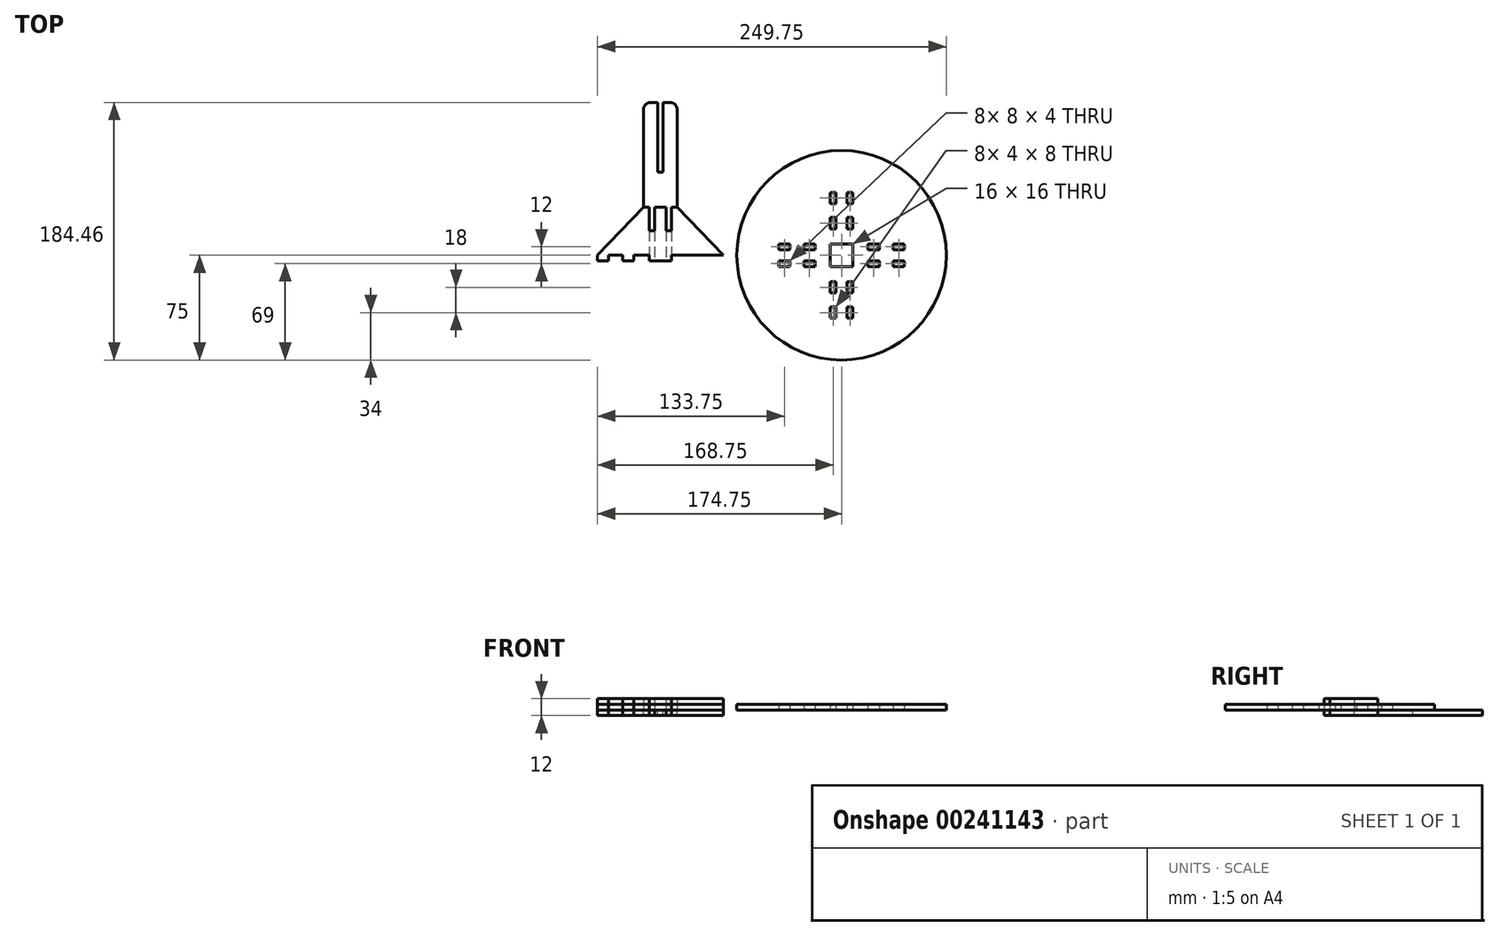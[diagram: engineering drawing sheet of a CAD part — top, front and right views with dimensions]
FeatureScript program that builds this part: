
annotation { "Feature Type Name" : "Feature", "Feature Type Description" : "" }
export const myFeature = defineFeature(function(context is Context, id is Id, definition is map)
    precondition{}
    {
        {
            var Q0;
            Q0=qCreatedBy(makeId("Top.planeOp"),FACE);
            var sketch = newSketch(context, id + "F0", { "sketchPlane" : qUnion([Q0])});
            skCircle(sketch, "E0", {"center": v(0, 0) * mm, "radius": 75 * mm});
            skLineSegment(sketch, "E1", {"start": v(-84.75, 0) * mm, "end": v(-129.75, 0) * mm});
            skLineSegment(sketch, "E2", {"start": v(-129.75, 0) * mm, "end": v(-129.75, 34.46) * mm});
            skLineSegment(sketch, "E3", {"start": v(-129.75, 34.46) * mm, "end": v(-117.75, 34.46) * mm});
            skLineSegment(sketch, "E4", {"start": v(-117.75, 34.46) * mm, "end": v(-84.75, 0) * mm});
            skLineSegment(sketch, "E5.top", {"start": v(-129.75, 17.59) * mm, "end": v(-125.75, 17.59) * mm});
            skLineSegment(sketch, "E5.right", {"start": v(-125.75, 34.46) * mm, "end": v(-125.75, 17.59) * mm});
            skLineSegment(sketch, "E6.bottom", {"start": v(-125.75, 34.46) * mm, "end": v(-121.75, 34.46) * mm});
            skLineSegment(sketch, "E6.top", {"start": v(-125.75, 0) * mm, "end": v(-121.75, 0) * mm});
            skLineSegment(sketch, "E6.left", {"start": v(-125.75, 34.46) * mm, "end": v(-125.75, 0) * mm});
            skLineSegment(sketch, "E6.right", {"start": v(-121.75, 34.46) * mm, "end": v(-121.75, 0) * mm});
            skLineSegment(sketch, "E7", {"start": v(-125.75, 17.59) * mm, "end": v(-121.75, 17.59) * mm});
            skLineSegment(sketch, "E8.bottom", {"start": v(-129.75, 0) * mm, "end": v(-121.75, 0) * mm});
            skLineSegment(sketch, "E8.top", {"start": v(-129.75, -4) * mm, "end": v(-121.75, -4) * mm});
            skLineSegment(sketch, "E8.left", {"start": v(-129.75, 0) * mm, "end": v(-129.75, -4) * mm});
            skLineSegment(sketch, "E8.right", {"start": v(-121.75, 0) * mm, "end": v(-121.75, -4) * mm});
            skLineSegment(sketch, "E9.bottom", {"start": v(-84.75, 0) * mm, "end": v(-92.75, 0) * mm});
            skLineSegment(sketch, "E9.top", {"start": v(-84.75, -4) * mm, "end": v(-92.75, -4) * mm});
            skLineSegment(sketch, "E9.left", {"start": v(-84.75, 0) * mm, "end": v(-84.75, -4) * mm});
            skLineSegment(sketch, "E9.right", {"start": v(-92.75, 0) * mm, "end": v(-92.75, -4) * mm});
            skLineSegment(sketch, "E10.bottom", {"start": v(-102.75, 0) * mm, "end": v(-110.75, 0) * mm});
            skLineSegment(sketch, "E10.top", {"start": v(-102.75, -4) * mm, "end": v(-110.75, -4) * mm});
            skLineSegment(sketch, "E10.left", {"start": v(-102.75, 0) * mm, "end": v(-102.75, -4) * mm});
            skLineSegment(sketch, "E10.right", {"start": v(-110.75, 0) * mm, "end": v(-110.75, -4) * mm});
            skLineSegment(sketch, "E11.MirrorCS", {"start": v(-174.75, 0) * mm, "end": v(-174.75, -4) * mm});
            skLineSegment(sketch, "E12.MirrorCS", {"start": v(-156.75, 0) * mm, "end": v(-156.75, -4) * mm});
            skLineSegment(sketch, "E13.MirrorCS", {"start": v(-148.75, 0) * mm, "end": v(-148.75, -4) * mm});
            skLineSegment(sketch, "E14.MirrorCS", {"start": v(-166.75, 0) * mm, "end": v(-166.75, -4) * mm});
            skLineSegment(sketch, "E15.MirrorCS", {"start": v(-137.75, 0) * mm, "end": v(-137.75, -4) * mm});
            skLineSegment(sketch, "E16.MirrorCS", {"start": v(-129.75, 0) * mm, "end": v(-137.75, 0) * mm});
            skLineSegment(sketch, "E17.MirrorCS", {"start": v(-133.75, 0) * mm, "end": v(-137.75, 0) * mm});
            skLineSegment(sketch, "E18.MirrorCS", {"start": v(-133.75, 34.46) * mm, "end": v(-137.75, 34.46) * mm});
            skLineSegment(sketch, "E19.MirrorCS", {"start": v(-129.75, 34.46) * mm, "end": v(-141.75, 34.46) * mm});
            skLineSegment(sketch, "E20.MirrorCS", {"start": v(-133.75, 17.59) * mm, "end": v(-137.75, 17.59) * mm});
            skLineSegment(sketch, "E21.MirrorCS", {"start": v(-129.75, 17.59) * mm, "end": v(-133.75, 17.59) * mm});
            skLineSegment(sketch, "E22.MirrorCS", {"start": v(-133.75, 34.46) * mm, "end": v(-133.75, 17.59) * mm});
            skLineSegment(sketch, "E23.MirrorCS", {"start": v(-156.75, -4) * mm, "end": v(-148.75, -4) * mm});
            skLineSegment(sketch, "E24.MirrorCS", {"start": v(-174.75, 0) * mm, "end": v(-166.75, 0) * mm});
            skLineSegment(sketch, "E25.MirrorCS", {"start": v(-156.75, 0) * mm, "end": v(-148.75, 0) * mm});
            skLineSegment(sketch, "E26.MirrorCS", {"start": v(-174.75, -4) * mm, "end": v(-166.75, -4) * mm});
            skLineSegment(sketch, "E27.MirrorCS", {"start": v(-129.75, -4) * mm, "end": v(-137.75, -4) * mm});
            skLineSegment(sketch, "E28.MirrorCS", {"start": v(-137.75, 34.46) * mm, "end": v(-137.75, 0) * mm});
            skLineSegment(sketch, "E29.MirrorCS", {"start": v(-133.75, 34.46) * mm, "end": v(-133.75, 0) * mm});
            skLineSegment(sketch, "E30.MirrorCS", {"start": v(-174.75, 0) * mm, "end": v(-129.75, 0) * mm});
            skLineSegment(sketch, "E31.MirrorCS", {"start": v(-141.75, 34.46) * mm, "end": v(-174.75, 0) * mm});
            skLineSegment(sketch, "E32", {"start": v(-133.75, 0) * mm, "end": v(-133.75, -4) * mm});
            skLineSegment(sketch, "E33", {"start": v(-125.75, 0) * mm, "end": v(-125.75, -4) * mm});
            skLineSegment(sketch, "E34.bottom", {"start": v(8, 4) * mm, "end": v(-8, 4) * mm, "construction": true});
            skLineSegment(sketch, "E34.top", {"start": v(8, -4) * mm, "end": v(-8, -4) * mm, "construction": true});
            skLineSegment(sketch, "E34.left", {"start": v(8, 4) * mm, "end": v(8, -4) * mm, "construction": true});
            skLineSegment(sketch, "E34.right", {"start": v(-8, 4) * mm, "end": v(-8, -4) * mm, "construction": true});
            skLineSegment(sketch, "E35.bottom", {"start": v(-8, 4) * mm, "end": v(8, 4) * mm});
            skLineSegment(sketch, "E35.top", {"start": v(-8, 8) * mm, "end": v(8, 8) * mm});
            skLineSegment(sketch, "E35.left", {"start": v(-8, 4) * mm, "end": v(-8, 8) * mm});
            skLineSegment(sketch, "E35.right", {"start": v(8, 4) * mm, "end": v(8, 8) * mm});
            skLineSegment(sketch, "E36", {"start": v(8, 8) * mm, "end": v(19, 8) * mm, "construction": true});
            skLineSegment(sketch, "E37", {"start": v(19, 8) * mm, "end": v(8, 0) * mm, "construction": true});
            skLineSegment(sketch, "E38", {"start": v(8, 0) * mm, "end": v(-47.74, 0) * mm, "construction": true});
            skLineSegment(sketch, "E39.bottom", {"start": v(19, 8) * mm, "end": v(27, 8) * mm});
            skLineSegment(sketch, "E39.top", {"start": v(19, 4) * mm, "end": v(27, 4) * mm});
            skLineSegment(sketch, "E39.left", {"start": v(19, 8) * mm, "end": v(19, 4) * mm});
            skLineSegment(sketch, "E39.right", {"start": v(27, 8) * mm, "end": v(27, 4) * mm});
            skLineSegment(sketch, "E40", {"start": v(27, 8) * mm, "end": v(37, 8) * mm, "construction": true});
            skLineSegment(sketch, "E41.bottom", {"start": v(37, 8) * mm, "end": v(45, 8) * mm});
            skLineSegment(sketch, "E41.top", {"start": v(37, 4) * mm, "end": v(45, 4) * mm});
            skLineSegment(sketch, "E41.left", {"start": v(37, 8) * mm, "end": v(37, 4) * mm});
            skLineSegment(sketch, "E41.right", {"start": v(45, 8) * mm, "end": v(45, 4) * mm});
            skLineSegment(sketch, "E42", {"start": v(0, 8) * mm, "end": v(0, -16.73) * mm, "construction": true});
            skPoint(sketch, "E42.endSnap0", {"position": v(0, 8) * mm});
            skLineSegment(sketch, "E43.MirrorCS", {"start": v(-45, 8) * mm, "end": v(-45, 4) * mm});
            skLineSegment(sketch, "E44.MirrorCS", {"start": v(-19, 8) * mm, "end": v(-19, 4) * mm});
            skLineSegment(sketch, "E45.MirrorCS", {"start": v(-27, 8) * mm, "end": v(-27, 4) * mm});
            skLineSegment(sketch, "E46.MirrorCS", {"start": v(-37, 8) * mm, "end": v(-37, 4) * mm});
            skLineSegment(sketch, "E47.MirrorCS", {"start": v(-19, 8) * mm, "end": v(-27, 8) * mm});
            skLineSegment(sketch, "E48.MirrorCS", {"start": v(-19, 4) * mm, "end": v(-27, 4) * mm});
            skLineSegment(sketch, "E49.MirrorCS", {"start": v(-37, 4) * mm, "end": v(-45, 4) * mm});
            skLineSegment(sketch, "E50.MirrorCS", {"start": v(-37, 8) * mm, "end": v(-45, 8) * mm});
            skLineSegment(sketch, "E51.MirrorCS", {"start": v(-27, 8) * mm, "end": v(-37, 8) * mm, "construction": true});
            skLineSegment(sketch, "E52.MirrorCS", {"start": v(8, -4) * mm, "end": v(8, -8) * mm});
            skLineSegment(sketch, "E53.MirrorCS", {"start": v(-27, -8) * mm, "end": v(-27, -4) * mm});
            skLineSegment(sketch, "E54.MirrorCS", {"start": v(27, -8) * mm, "end": v(27, -4) * mm});
            skLineSegment(sketch, "E55.MirrorCS", {"start": v(-45, -8) * mm, "end": v(-45, -4) * mm});
            skLineSegment(sketch, "E56.MirrorCS", {"start": v(19, -8) * mm, "end": v(19, -4) * mm});
            skLineSegment(sketch, "E57.MirrorCS", {"start": v(-19, -8) * mm, "end": v(-19, -4) * mm});
            skLineSegment(sketch, "E58.MirrorCS", {"start": v(-8, -4) * mm, "end": v(-8, -8) * mm});
            skLineSegment(sketch, "E59.MirrorCS", {"start": v(37, -8) * mm, "end": v(37, -4) * mm});
            skLineSegment(sketch, "E60.MirrorCS", {"start": v(45, -8) * mm, "end": v(45, -4) * mm});
            skLineSegment(sketch, "E61.MirrorCS", {"start": v(-37, -8) * mm, "end": v(-37, -4) * mm});
            skLineSegment(sketch, "E62.MirrorCS", {"start": v(-8, -4) * mm, "end": v(8, -4) * mm});
            skLineSegment(sketch, "E63.MirrorCS", {"start": v(19, -8) * mm, "end": v(27, -8) * mm});
            skLineSegment(sketch, "E64.MirrorCS", {"start": v(19, -4) * mm, "end": v(27, -4) * mm});
            skLineSegment(sketch, "E65.MirrorCS", {"start": v(-37, -8) * mm, "end": v(-45, -8) * mm});
            skLineSegment(sketch, "E66.MirrorCS", {"start": v(-8, -8) * mm, "end": v(8, -8) * mm});
            skLineSegment(sketch, "E67.MirrorCS", {"start": v(-37, -4) * mm, "end": v(-45, -4) * mm});
            skLineSegment(sketch, "E68.MirrorCS", {"start": v(-27, -8) * mm, "end": v(-37, -8) * mm, "construction": true});
            skPoint(sketch, "E69.MirrorP", {"position": v(0, -8) * mm});
            skLineSegment(sketch, "E70.MirrorCS", {"start": v(27, -8) * mm, "end": v(37, -8) * mm, "construction": true});
            skLineSegment(sketch, "E71.MirrorCS", {"start": v(37, -8) * mm, "end": v(45, -8) * mm});
            skLineSegment(sketch, "E72.MirrorCS", {"start": v(-19, -8) * mm, "end": v(-27, -8) * mm});
            skLineSegment(sketch, "E73.MirrorCS", {"start": v(-19, -4) * mm, "end": v(-27, -4) * mm});
            skLineSegment(sketch, "E74.MirrorCS", {"start": v(8, -8) * mm, "end": v(19, -8) * mm, "construction": true});
            skLineSegment(sketch, "E75.MirrorCS", {"start": v(37, -4) * mm, "end": v(45, -4) * mm});
            skLineSegment(sketch, "E76.bottom", {"start": v(-8, 4) * mm, "end": v(-4, 4) * mm});
            skLineSegment(sketch, "E76.top", {"start": v(-8, -4) * mm, "end": v(-4, -4) * mm});
            skLineSegment(sketch, "E76.left", {"start": v(-8, 4) * mm, "end": v(-8, -4) * mm});
            skLineSegment(sketch, "E76.right", {"start": v(-4, 4) * mm, "end": v(-4, -4) * mm});
            skLineSegment(sketch, "E77.bottom", {"start": v(8, 4) * mm, "end": v(8, 4) * mm});
            skLineSegment(sketch, "E77.top", {"start": v(8, -4) * mm, "end": v(8, -4) * mm});
            skLineSegment(sketch, "E77.left", {"start": v(8, 4) * mm, "end": v(8, -4) * mm});
            skLineSegment(sketch, "E77.right", {"start": v(8, 4) * mm, "end": v(8, -4) * mm});
            skLineSegment(sketch, "E78", {"start": v(-8, 8) * mm, "end": v(-8, 19) * mm, "construction": true});
            skLineSegment(sketch, "E79", {"start": v(-8, 19) * mm, "end": v(-8, 27) * mm, "construction": true});
            skLineSegment(sketch, "E80.bottom", {"start": v(-8, 27) * mm, "end": v(-4, 27) * mm});
            skLineSegment(sketch, "E80.top", {"start": v(-8, 19) * mm, "end": v(-4, 19) * mm});
            skLineSegment(sketch, "E80.left", {"start": v(-8, 27) * mm, "end": v(-8, 19) * mm});
            skLineSegment(sketch, "E80.right", {"start": v(-4, 27) * mm, "end": v(-4, 19) * mm});
            skLineSegment(sketch, "E81.bottom", {"start": v(-8, 37) * mm, "end": v(-4, 37) * mm});
            skLineSegment(sketch, "E81.top", {"start": v(-8, 45) * mm, "end": v(-4, 45) * mm});
            skLineSegment(sketch, "E81.left", {"start": v(-8, 37) * mm, "end": v(-8, 45) * mm});
            skLineSegment(sketch, "E81.right", {"start": v(-4, 37) * mm, "end": v(-4, 45) * mm});
            skLineSegment(sketch, "E82.MirrorCS", {"start": v(-8, -27) * mm, "end": v(-4, -27) * mm});
            skLineSegment(sketch, "E83.MirrorCS", {"start": v(-8, -19) * mm, "end": v(-4, -19) * mm});
            skLineSegment(sketch, "E84.MirrorCS", {"start": v(-8, -27) * mm, "end": v(-8, -19) * mm});
            skLineSegment(sketch, "E85.MirrorCS", {"start": v(-8, -37) * mm, "end": v(-8, -45) * mm});
            skLineSegment(sketch, "E86.MirrorCS", {"start": v(-4, -37) * mm, "end": v(-4, -45) * mm});
            skLineSegment(sketch, "E87.MirrorCS", {"start": v(-8, -45) * mm, "end": v(-4, -45) * mm});
            skLineSegment(sketch, "E88.MirrorCS", {"start": v(-8, -19) * mm, "end": v(-8, -27) * mm, "construction": true});
            skLineSegment(sketch, "E89.MirrorCS", {"start": v(-8, -37) * mm, "end": v(-4, -37) * mm});
            skLineSegment(sketch, "E90.MirrorCS", {"start": v(-4, -27) * mm, "end": v(-4, -19) * mm});
            skLineSegment(sketch, "E91.MirrorCS", {"start": v(8, 27) * mm, "end": v(4, 27) * mm});
            skLineSegment(sketch, "E92.MirrorCS", {"start": v(8, 37) * mm, "end": v(4, 37) * mm});
            skLineSegment(sketch, "E93.MirrorCS", {"start": v(8, 45) * mm, "end": v(4, 45) * mm});
            skLineSegment(sketch, "E94.MirrorCS", {"start": v(8, 19) * mm, "end": v(4, 19) * mm});
            skLineSegment(sketch, "E95.MirrorCS", {"start": v(8, 27) * mm, "end": v(8, 19) * mm});
            skLineSegment(sketch, "E96.MirrorCS", {"start": v(4, 37) * mm, "end": v(4, 45) * mm});
            skLineSegment(sketch, "E97.MirrorCS", {"start": v(8, 19) * mm, "end": v(8, 27) * mm, "construction": true});
            skLineSegment(sketch, "E98.MirrorCS", {"start": v(4, 27) * mm, "end": v(4, 19) * mm});
            skLineSegment(sketch, "E99.MirrorCS", {"start": v(8, 37) * mm, "end": v(8, 45) * mm});
            skLineSegment(sketch, "E100.MirrorCS", {"start": v(4, 4) * mm, "end": v(4, -4) * mm});
            skLineSegment(sketch, "E101.MirrorCS", {"start": v(8, -45) * mm, "end": v(4, -45) * mm});
            skLineSegment(sketch, "E102.MirrorCS", {"start": v(8, -19) * mm, "end": v(4, -19) * mm});
            skLineSegment(sketch, "E103.MirrorCS", {"start": v(8, -37) * mm, "end": v(4, -37) * mm});
            skLineSegment(sketch, "E104.MirrorCS", {"start": v(8, -27) * mm, "end": v(8, -19) * mm});
            skLineSegment(sketch, "E105.MirrorCS", {"start": v(4, -37) * mm, "end": v(4, -45) * mm});
            skLineSegment(sketch, "E106.MirrorCS", {"start": v(8, -37) * mm, "end": v(8, -45) * mm});
            skLineSegment(sketch, "E107.MirrorCS", {"start": v(8, -27) * mm, "end": v(4, -27) * mm});
            skLineSegment(sketch, "E108.MirrorCS", {"start": v(4, -27) * mm, "end": v(4, -19) * mm});
            skLineSegment(sketch, "E109.MirrorCS", {"start": v(8, -19) * mm, "end": v(8, -27) * mm, "construction": true});
            skLineSegment(sketch, "E110.bottom", {"start": v(-141.75, 34.46) * mm, "end": v(-117.75, 34.46) * mm});
            skLineSegment(sketch, "E110.top", {"start": v(-136.75, 109.46) * mm, "end": v(-122.75, 109.46) * mm});
            skLineSegment(sketch, "E110.left", {"start": v(-141.75, 34.46) * mm, "end": v(-141.75, 104.46) * mm});
            skLineSegment(sketch, "E110.right", {"start": v(-117.75, 34.46) * mm, "end": v(-117.75, 104.46) * mm});
            skLineSegment(sketch, "E111.bottom", {"start": v(-129.75, 109.46) * mm, "end": v(-127.75, 109.46) * mm});
            skLineSegment(sketch, "E111.top", {"start": v(-129.75, 59.46) * mm, "end": v(-127.75, 59.46) * mm});
            skLineSegment(sketch, "E111.left", {"start": v(-129.75, 109.46) * mm, "end": v(-129.75, 59.46) * mm});
            skLineSegment(sketch, "E111.right", {"start": v(-127.75, 109.46) * mm, "end": v(-127.75, 59.46) * mm});
            skLineSegment(sketch, "E112.MirrorCS", {"start": v(-131.75, 109.46) * mm, "end": v(-131.75, 59.46) * mm});
            skLineSegment(sketch, "E113.MirrorCS", {"start": v(-129.75, 59.46) * mm, "end": v(-131.75, 59.46) * mm});
            skPoint(sketch, "E114.visualSharp", {"position": v(-141.75, 109.46) * mm});
            skArc(sketch, "E114.filletArc", {"start": v(-136.75, 109.46) * mm, "mid": v(-140.29, 108) * mm, "end": v(-141.75, 104.46) * mm});
            skPoint(sketch, "E115.visualSharp", {"position": v(-117.75, 109.46) * mm});
            skArc(sketch, "E115.filletArc", {"start": v(-117.75, 104.46) * mm, "mid": v(-119.21, 108) * mm, "end": v(-122.75, 109.46) * mm});
            skSolve(sketch);
        }
        {
            var Q0;
            {var subQ0=sQuery(id+"F0.wireOp",EDGE,"E11.MirrorCS");Q0=makeQuery(id+"F0.imprint","IMPRINT",FACE,{"disambiguationData":[TD([[makeQuery(id+"F0.imprint","IMPRINT",EDGE,{"derivedFrom":subQ0}),1.0]])]});}
            var Q1;
            {var subQ0=sQuery(id+"F0.wireOp",EDGE,"E31.MirrorCS");Q1=makeQuery(id+"F0.imprint","IMPRINT",FACE,{"disambiguationData":[TD([[makeQuery(id+"F0.imprint","IMPRINT",EDGE,{"derivedFrom":subQ0}),1.0]])]});}
            var Q2;
            {var subQ0=sQuery(id+"F0.wireOp",EDGE,"E12.MirrorCS");Q2=makeQuery(id+"F0.imprint","IMPRINT",FACE,{"disambiguationData":[TD([[makeQuery(id+"F0.imprint","IMPRINT",EDGE,{"derivedFrom":subQ0}),1.0]])]});}
            var Q3;
            {var subQ0=sQuery(id+"F0.wireOp",EDGE,"E20.MirrorCS");Q3=makeQuery(id+"F0.imprint","IMPRINT",FACE,{"disambiguationData":[TD([[makeQuery(id+"F0.imprint","IMPRINT",EDGE,{"derivedFrom":subQ0}),1.0]])]});}
            var Q4;
            {var subQ3=sQuery(id+"F0.wireOp",EDGE,"E21.MirrorCS");Q4=makeQuery(id+"F0.imprint","IMPRINT",FACE,{"disambiguationData":[TD([[makeQuery(id+"F0.imprint","IMPRINT",EDGE,{"derivedFrom":subQ3}),1.0]])]});}
            var Q5;
            {var subQ3=sQuery(id+"F0.wireOp",EDGE,"E21.MirrorCS");Q5=makeQuery(id+"F0.imprint","IMPRINT",FACE,{"disambiguationData":[TD([[makeQuery(id+"F0.imprint","IMPRINT",EDGE,{"derivedFrom":subQ3}),-1.0]])]});}
            var Q6;
            {var subQ3=sQuery(id+"F0.wireOp",EDGE,"E5.top");Q6=makeQuery(id+"F0.imprint","IMPRINT",FACE,{"disambiguationData":[TD([[makeQuery(id+"F0.imprint","IMPRINT",EDGE,{"derivedFrom":subQ3}),1.0]])]});}
            var Q7;
            {var subQ3=sQuery(id+"F0.wireOp",EDGE,"E5.top");Q7=makeQuery(id+"F0.imprint","IMPRINT",FACE,{"disambiguationData":[TD([[makeQuery(id+"F0.imprint","IMPRINT",EDGE,{"derivedFrom":subQ3}),-1.0]])]});}
            var Q8;
            {var subQ0=sQuery(id+"F0.wireOp",EDGE,"E7");Q8=makeQuery(id+"F0.imprint","IMPRINT",FACE,{"disambiguationData":[TD([[makeQuery(id+"F0.imprint","IMPRINT",EDGE,{"derivedFrom":subQ0}),-1.0]])]});}
            var Q9;
            {var subQ0=sQuery(id+"F0.wireOp",EDGE,"E4");Q9=makeQuery(id+"F0.imprint","IMPRINT",FACE,{"disambiguationData":[TD([[makeQuery(id+"F0.imprint","IMPRINT",EDGE,{"derivedFrom":subQ0}),-1.0]])]});}
            var Q10;
            Q10=makeQuery(id+"F0.imprint","IMPRINT",FACE,{"disambiguationData":[TD([[makeQuery(id+"F0.imprint","IMPRINT",EDGE,{"derivedFrom":sQuery(id+"F0.wireOp",EDGE,"E10.bottom")}),1.0]])]});
            var Q11;
            Q11=makeQuery(id+"F0.imprint","IMPRINT",FACE,{"disambiguationData":[TD([[makeQuery(id+"F0.imprint","IMPRINT",EDGE,{"derivedFrom":sQuery(id+"F0.wireOp",EDGE,"E9.bottom")}),1.0]])]});
            var Q12;
            {var subQ0=sQuery(id+"F0.wireOp",EDGE,"E15.MirrorCS");Q12=makeQuery(id+"F0.imprint","IMPRINT",FACE,{"disambiguationData":[TD([[makeQuery(id+"F0.imprint","IMPRINT",EDGE,{"derivedFrom":subQ0}),1.0]])]});}
            var Q13;
            {var subQ0=sQuery(id+"F0.wireOp",EDGE,"E8.left");Q13=makeQuery(id+"F0.imprint","IMPRINT",FACE,{"disambiguationData":[TD([[makeQuery(id+"F0.imprint","IMPRINT",EDGE,{"derivedFrom":subQ0}),-1.0]])]});}
            var Q14;
            {var subQ0=sQuery(id+"F0.wireOp",EDGE,"E8.left");Q14=makeQuery(id+"F0.imprint","IMPRINT",FACE,{"disambiguationData":[TD([[makeQuery(id+"F0.imprint","IMPRINT",EDGE,{"derivedFrom":subQ0}),1.0]])]});}
            var Q15;
            {var subQ0=sQuery(id+"F0.wireOp",EDGE,"E8.right");Q15=makeQuery(id+"F0.imprint","IMPRINT",FACE,{"disambiguationData":[TD([[makeQuery(id+"F0.imprint","IMPRINT",EDGE,{"derivedFrom":subQ0}),-1.0]])]});}
            var Q16;
            Q16=makeQuery(id+"F0.imprint","IMPRINT",FACE,{"disambiguationData":[TD([[makeQuery(id+"F0.imprint","IMPRINT",EDGE,{"derivedFrom":sQuery(id+"F0.wireOp",EDGE,"E0")}),1.0]])]});
            extrude(context, id + "F1", {"entities" : qUnion([Q0, Q1, Q2, Q3, Q4, Q5, Q6, Q7, Q8, Q9, Q10, Q11, Q12, Q13, Q14, Q15, Q16]), "depth" : 4 * mm});
        }
        {
            var Q0;
            {var subQ0=sQuery(id+"F0.wireOp",EDGE,"E11.MirrorCS");Q0=makeQuery(id+"F0.imprint","IMPRINT",FACE,{"disambiguationData":[TD([[makeQuery(id+"F0.imprint","IMPRINT",EDGE,{"derivedFrom":subQ0}),1.0]])]});}
            var Q1;
            {var subQ0=sQuery(id+"F0.wireOp",EDGE,"E31.MirrorCS");Q1=makeQuery(id+"F0.imprint","IMPRINT",FACE,{"disambiguationData":[TD([[makeQuery(id+"F0.imprint","IMPRINT",EDGE,{"derivedFrom":subQ0}),1.0]])]});}
            var Q2;
            {var subQ0=sQuery(id+"F0.wireOp",EDGE,"E12.MirrorCS");Q2=makeQuery(id+"F0.imprint","IMPRINT",FACE,{"disambiguationData":[TD([[makeQuery(id+"F0.imprint","IMPRINT",EDGE,{"derivedFrom":subQ0}),1.0]])]});}
            var Q3;
            {var subQ3=sQuery(id+"F0.wireOp",EDGE,"E21.MirrorCS");Q3=makeQuery(id+"F0.imprint","IMPRINT",FACE,{"disambiguationData":[TD([[makeQuery(id+"F0.imprint","IMPRINT",EDGE,{"derivedFrom":subQ3}),-1.0]])]});}
            var Q4;
            {var subQ3=sQuery(id+"F0.wireOp",EDGE,"E5.top");Q4=makeQuery(id+"F0.imprint","IMPRINT",FACE,{"disambiguationData":[TD([[makeQuery(id+"F0.imprint","IMPRINT",EDGE,{"derivedFrom":subQ3}),1.0]])]});}
            var Q5;
            {var subQ3=sQuery(id+"F0.wireOp",EDGE,"E5.top");Q5=makeQuery(id+"F0.imprint","IMPRINT",FACE,{"disambiguationData":[TD([[makeQuery(id+"F0.imprint","IMPRINT",EDGE,{"derivedFrom":subQ3}),-1.0]])]});}
            var Q6;
            {var subQ3=sQuery(id+"F0.wireOp",EDGE,"E21.MirrorCS");Q6=makeQuery(id+"F0.imprint","IMPRINT",FACE,{"disambiguationData":[TD([[makeQuery(id+"F0.imprint","IMPRINT",EDGE,{"derivedFrom":subQ3}),1.0]])]});}
            var Q7;
            {var subQ0=sQuery(id+"F0.wireOp",EDGE,"E8.left");Q7=makeQuery(id+"F0.imprint","IMPRINT",FACE,{"disambiguationData":[TD([[makeQuery(id+"F0.imprint","IMPRINT",EDGE,{"derivedFrom":subQ0}),-1.0]])]});}
            var Q8;
            {var subQ0=sQuery(id+"F0.wireOp",EDGE,"E8.left");Q8=makeQuery(id+"F0.imprint","IMPRINT",FACE,{"disambiguationData":[TD([[makeQuery(id+"F0.imprint","IMPRINT",EDGE,{"derivedFrom":subQ0}),1.0]])]});}
            var Q9;
            {var subQ5=sQuery(id+"F0.wireOp",EDGE,"E20.MirrorCS");Q9=makeQuery(id+"F0.imprint","IMPRINT",FACE,{"disambiguationData":[TD([[makeQuery(id+"F0.imprint","IMPRINT",EDGE,{"derivedFrom":subQ5}),-1.0]])]});}
            var Q10;
            {var subQ0=sQuery(id+"F0.wireOp",EDGE,"E6.bottom");Q10=makeQuery(id+"F0.imprint","IMPRINT",FACE,{"disambiguationData":[TD([[makeQuery(id+"F0.imprint","IMPRINT",EDGE,{"derivedFrom":subQ0}),-1.0]])]});}
            var Q11;
            {var subQ0=sQuery(id+"F0.wireOp",EDGE,"E4");Q11=makeQuery(id+"F0.imprint","IMPRINT",FACE,{"disambiguationData":[TD([[makeQuery(id+"F0.imprint","IMPRINT",EDGE,{"derivedFrom":subQ0}),-1.0]])]});}
            var Q12;
            Q12=makeQuery(id+"F0.imprint","IMPRINT",FACE,{"disambiguationData":[TD([[makeQuery(id+"F0.imprint","IMPRINT",EDGE,{"derivedFrom":sQuery(id+"F0.wireOp",EDGE,"E10.bottom")}),1.0]])]});
            var Q13;
            Q13=makeQuery(id+"F0.imprint","IMPRINT",FACE,{"disambiguationData":[TD([[makeQuery(id+"F0.imprint","IMPRINT",EDGE,{"derivedFrom":sQuery(id+"F0.wireOp",EDGE,"E9.bottom")}),1.0]])]});
            var Q14;
            {var subQ0=sQuery(id+"F0.wireOp",EDGE,"E7");Q14=makeQuery(id+"F0.imprint","IMPRINT",FACE,{"disambiguationData":[TD([[makeQuery(id+"F0.imprint","IMPRINT",EDGE,{"derivedFrom":subQ0}),1.0]])]});}
            var Q15;
            {var subQ4=sQuery(id+"F0.wireOp",EDGE,"E110.left");Q15=makeQuery(id+"F0.imprint","IMPRINT",FACE,{"disambiguationData":[TD([[makeQuery(id+"F0.imprint","IMPRINT",EDGE,{"derivedFrom":subQ4}),-1.0]])]});}
            extrude(context, id + "F2", {"entities" : qUnion([Q0, Q1, Q2, Q3, Q4, Q5, Q6, Q7, Q8, Q9, Q10, Q11, Q12, Q13, Q14, Q15]), "oppositeDirection" : true, "depth" : 4 * mm});
        }
        {
            var Q0;
            Q0=makeQuery(id+"F1.opExtrude","CAP_FACE",FACE,{"disambiguationData":[OSD([sQuery(id+"F0.wireOp",EDGE,"E1"),sQuery(id+"F0.wireOp",EDGE,"E4"),sQuery(id+"F0.wireOp",EDGE,"E6.left"),sQuery(id+"F0.wireOp",EDGE,"E6.right"),sQuery(id+"F0.wireOp",EDGE,"E7"),sQuery(id+"F0.wireOp",EDGE,"E8.top"),sQuery(id+"F0.wireOp",EDGE,"E8.right"),sQuery(id+"F0.wireOp",EDGE,"E9.top"),sQuery(id+"F0.wireOp",EDGE,"E9.left"),sQuery(id+"F0.wireOp",EDGE,"E9.right"),sQuery(id+"F0.wireOp",EDGE,"E10.top"),sQuery(id+"F0.wireOp",EDGE,"E10.left"),sQuery(id+"F0.wireOp",EDGE,"E10.right"),sQuery(id+"F0.wireOp",EDGE,"E11.MirrorCS"),sQuery(id+"F0.wireOp",EDGE,"E12.MirrorCS"),sQuery(id+"F0.wireOp",EDGE,"E13.MirrorCS"),sQuery(id+"F0.wireOp",EDGE,"E14.MirrorCS"),sQuery(id+"F0.wireOp",EDGE,"E15.MirrorCS"),sQuery(id+"F0.wireOp",EDGE,"E20.MirrorCS"),sQuery(id+"F0.wireOp",EDGE,"E23.MirrorCS"),sQuery(id+"F0.wireOp",EDGE,"E26.MirrorCS"),sQuery(id+"F0.wireOp",EDGE,"E27.MirrorCS"),sQuery(id+"F0.wireOp",EDGE,"E28.MirrorCS"),sQuery(id+"F0.wireOp",EDGE,"E29.MirrorCS"),sQuery(id+"F0.wireOp",EDGE,"E30.MirrorCS"),sQuery(id+"F0.wireOp",EDGE,"E31.MirrorCS"),sQuery(id+"F0.wireOp",EDGE,"E110.bottom")])],"isStart":false});
            var sketch = newSketch(context, id + "F3", { "sketchPlane" : qUnion([Q0])});
            skArc(sketch, "E116", {"start": v(-174.75, -4) * mm, "mid": v(-129.75, -49) * mm, "end": v(-84.75, -4) * mm});
            skSolve(sketch);
        }
        {
            var Q0;
            Q0=makeQuery(id+"F3.imprint","IMPRINT",FACE,{"disambiguationData":[TD([[makeQuery(id+"F3.imprint","IMPRINT",EDGE,{"derivedFrom":sQuery(id+"F3.wireOp",EDGE,"E116")}),1.0]])]});
            var Q1;
            {var subQ9=sQuery(id+"F0.wireOp",EDGE,"E4");Q1=makeQuery(id+"F3.imprint","IMPRINT",FACE,{"disambiguationData":[TD([[makeQuery(id+"F3.imprint","IMPRINT",EDGE,{"derivedFrom":makeQuery(id+"F1.opExtrude","CAP_EDGE",EDGE,{"disambiguationData":[OSD([subQ9])],"isStart":false})}),-1.0]])]});}
            extrude(context, id + "F4", {"entities" : qUnion([Q0, Q1]), "depth" : 4 * mm});
        }
    });
